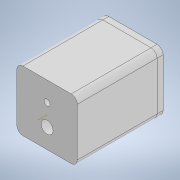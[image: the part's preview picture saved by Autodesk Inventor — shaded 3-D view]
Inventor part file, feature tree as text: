
AUTODESK INVENTOR PART (.ipt)
format: ipt  version: 2022 (Build 260153000, 153)  size: 21,289,984 bytes
history: native  units: mm
features: sketch x6, projected_geometry x4, other x3, extrude x3, move_body x2, hole x2, direct_edit x1, fillet x1, boolean_combine x1, revolve x1, sweep x1, pattern_circular x1, thicken_offset x1
ambient origin geometry x8: Origin, YZ Plane, XZ Plane, XY Plane, X Axis, Y Axis, Z Axis, Center Point
bodies: Solid1 (feature_tree), Solid2 (feature_tree), Solid3 (feature_tree)
feature tree (27):
  other  "MeshFeature1"
  direct_edit  "Direct Edit1"
  move_body  "Move Body1"
  move_body  "Move Body2"
  sketch  "Sketch1"  dims[d0=6.7mm d1=10.0mm d2=10.0mm d3=1.805mm d4=0.088mm d5=0.0mm d6=40.0mm]
  extrude  "Extrusion1"  Depth=10.0mm TaperAngle=0.0deg
  fillet  "Fillet1"  Radius=40.0mm
  extrude  "Extrusion2"  Depth=5.0mm
  boolean_combine  "Combine1"
  revolve  "Revolution1"  [1 undecoded]
  sweep  "Sweep1"
  extrude  "Extrusion3"  Depth=4.0mm TaperAngle=0.0deg
  other  "Work Axis1"
  pattern_circular  "Circular Pattern1"  [2 undecoded]
  thicken_offset  "Thicken1"
  hole  "Hole1"  [1 undecoded]
  hole  "Hole2"  [1 undecoded]
  sketch  "Sketch2"  dims[d7=0.0mm d8=-0.176mm d9=0.0mm d10=135.0deg d11=5.0mm]
  projected_geometry  "Projected Loop1"
  sketch  "Sketch3"  dims[d12=5.0mm d13=4.0mm]
  sketch  "Sketch4"  dims[d14=5.0mm d15=3.0mm]
  projected_geometry  "Projected Loop2"
  sketch  "Sketch5"  dims[d16=4.0mm d17=40.0mm d18=0.0mm]
  projected_geometry  "Projected Loop3"
  sketch  "Sketch6"  dims[d19=4.0mm d20=4.0mm d21=0.0mm d22=90.0deg d23=8.0mm d24=0.0mm d25=0.0mm d26=4.0mm d27=0.0mm d28=20.0mm d29=360.0deg d31=2.0mm d32=2.0mm d33=3.4mm d34=6.0mm d35=6.3mm d36=2.0mm d37=90.0deg d38=14.0mm d39=0.0mm d42=4.0mm d43=6.0mm d44=6.3mm d45=2.0mm d46=90.0deg d47=14.0mm d48=0.0mm]
  projected_geometry  "Projected Loop4"
  other  "Scale1"
note: 5 required parameter values undecoded (feature->parameter linkage not recoverable at this tier; creation-order binding heuristic only, values carry confidence <= 0.55)